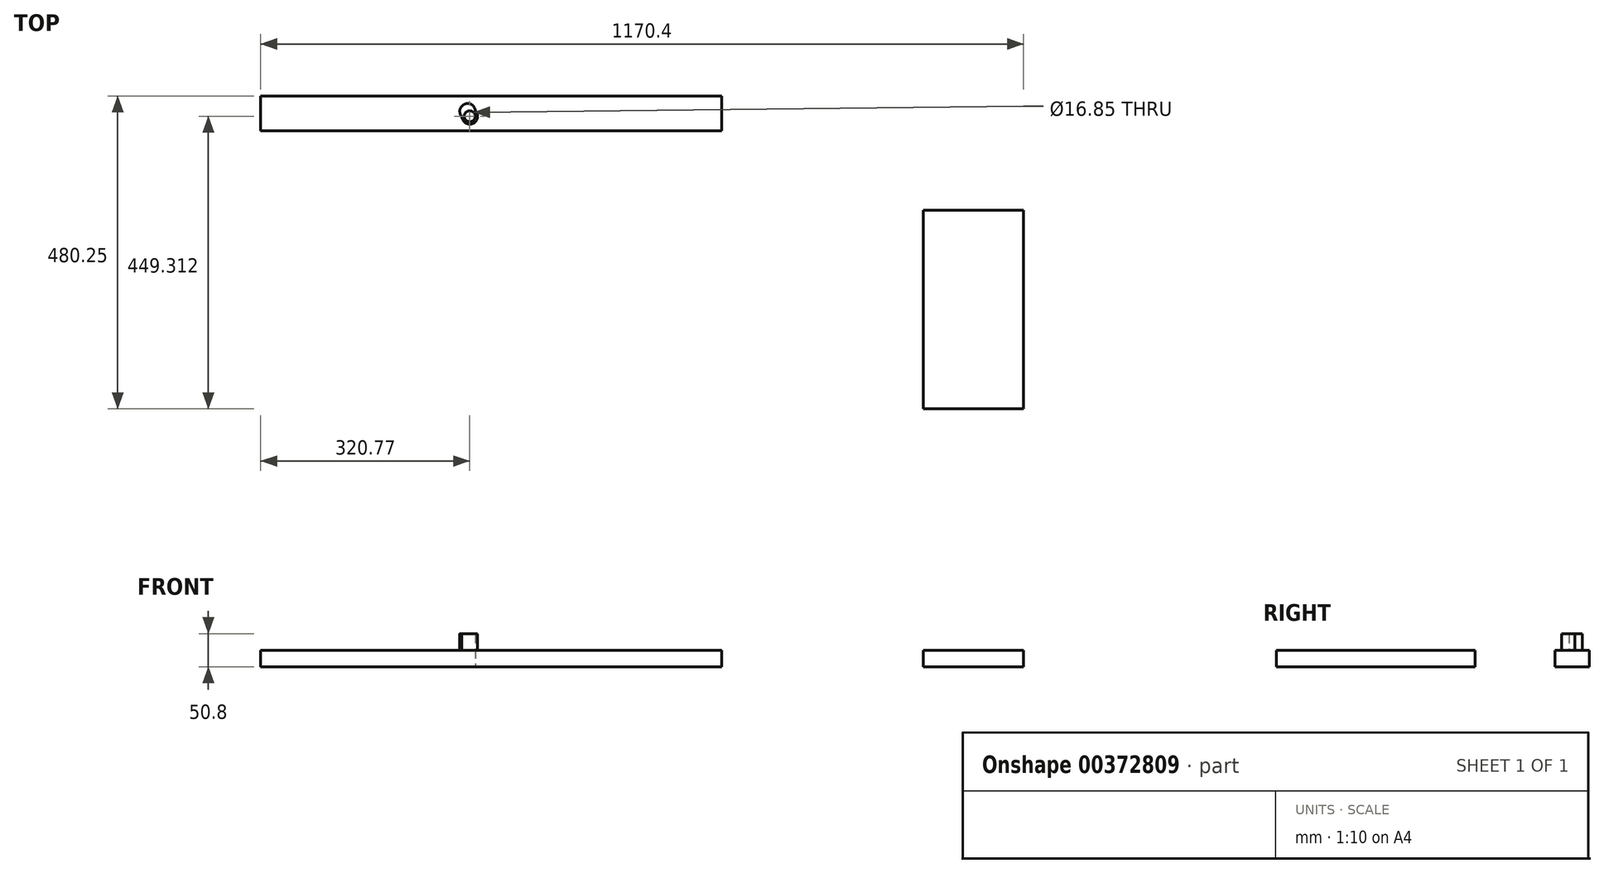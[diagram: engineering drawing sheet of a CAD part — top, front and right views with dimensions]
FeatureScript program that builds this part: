
annotation { "Feature Type Name" : "Feature", "Feature Type Description" : "" }
export const myFeature = defineFeature(function(context is Context, id is Id, definition is map)
    precondition{}
    {
        {
            var Q0;
            Q0=qCreatedBy(makeId("Top.planeOp"),FACE);
            var sketch = newSketch(context, id + "F0", { "sketchPlane" : qUnion([Q0])});
            skLineSegment(sketch, "E0.bottom", {"start": v(309.62, 304.8) * mm, "end": v(463.46, 304.8) * mm});
            skLineSegment(sketch, "E0.top", {"start": v(309.62, 0) * mm, "end": v(463.46, 0) * mm});
            skLineSegment(sketch, "E0.left", {"start": v(309.62, 304.8) * mm, "end": v(309.62, 0) * mm});
            skLineSegment(sketch, "E0.right", {"start": v(463.46, 304.8) * mm, "end": v(463.46, 0) * mm});
            skLineSegment(sketch, "E1.bottom", {"start": v(-706.94, 427.27) * mm, "end": v(0, 427.27) * mm});
            skLineSegment(sketch, "E1.top", {"start": v(-706.94, 480.25) * mm, "end": v(0, 480.25) * mm});
            skLineSegment(sketch, "E1.left", {"start": v(-706.94, 427.27) * mm, "end": v(-706.94, 480.25) * mm});
            skLineSegment(sketch, "E1.right", {"start": v(0, 427.27) * mm, "end": v(0, 480.25) * mm});
            skSolve(sketch);
        }
        {
            var Q0;
            Q0 = qSketchRegion(id + "F0", true);
            extrude(context, id + "F1", {"entities" : qUnion([Q0]), "depth" : 25.4 * mm});
        }
        {
            var Q0;
            Q0=makeQuery(id+"F1.opExtrude","CAP_FACE",FACE,{"disambiguationData":[OSD([sQuery(id+"F0.wireOp",EDGE,"E1.bottom"),sQuery(id+"F0.wireOp",EDGE,"E1.top"),sQuery(id+"F0.wireOp",EDGE,"E1.left"),sQuery(id+"F0.wireOp",EDGE,"E1.right")])],"isStart":false});
            var sketch = newSketch(context, id + "F2", { "sketchPlane" : qUnion([Q0])});
            skCircle(sketch, "E2", {"center": v(-386.17, 449.31) * mm, "radius": 12.08 * mm});
            skCircle(sketch, "E3", {"center": v(-386.17, 449.31) * mm, "radius": 8.42 * mm});
            skCircle(sketch, "E4", {"center": v(-389.52, 456.96) * mm, "radius": 11.94 * mm});
            skSolve(sketch);
        }
        {
            var Q0;
            Q0 = qSketchRegion(id + "F2", true);
            extrude(context, id + "F3", {"entities" : qUnion([Q0]), "operationType" : NewBodyOperationType.ADD, "depth" : 25.4 * mm});
        }
        {
            var Q0;
            Q0=makeQuery(id+"F3.boolean.opBoolean","SPLIT",FACE,{"disambiguationData":[TD([makeQuery(id+"F3.opExtrude","SWEPT_FACE",FACE,{"disambiguationData":[OSD([sQuery(id+"F2.wireOp",EDGE,"E3")])]})])],"derivedFrom":makeQuery(id+"F1.opExtrude","CAP_FACE",FACE,{"disambiguationData":[OSD([sQuery(id+"F0.wireOp",EDGE,"E1.bottom"),sQuery(id+"F0.wireOp",EDGE,"E1.top"),sQuery(id+"F0.wireOp",EDGE,"E1.left"),sQuery(id+"F0.wireOp",EDGE,"E1.right")])],"isStart":false})});
            extrude(context, id + "F4", {"entities" : qUnion([Q0]), "operationType" : NewBodyOperationType.REMOVE, "endBound" : BoundingType.THROUGH_ALL, "oppositeDirection" : true, "depth" : 25.4 * mm});
        }
    });
